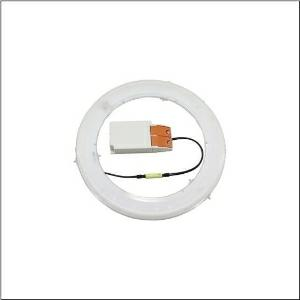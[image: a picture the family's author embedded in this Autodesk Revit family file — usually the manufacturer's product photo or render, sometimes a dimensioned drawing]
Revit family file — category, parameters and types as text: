
# Revit family: lunis_r_58dc011d04300a
name_source: partatom
category: Lighting Fixtures
units: mm (PartAtom-declared; Revit-internal decimal feet)

## family parameters
Cut with Voids When Loaded = No
Host = Face
Light Source = No
Part Type = Normal
Room Calculation Point = No
Round Connector Dimension = Use Diameter
Shared = No

## types (1)
- Lunis R (1 x LED, 4400 lm, 25.3 W, 4000K)
    Apparent Load = 25 VA
    CIE Flux Codes = 61 91 99 100 100
    Color Rendering = 80
    Color Temperature = 4000K
    Default Elevation = 1800 mm
    Description = Lunis R, luminaire insert, rated luminous flux: 4.400lm, light colour: 840, control gear: DALI 2, mains connection: 220..240V, AC, 50/60Hz, rated input power: 25W, primary light control with lens, of plastic, primary optical cover: cover, of PMMA, light emission: direct distribution, protection rating (complete): IP20, certification: CE, packaging unit: 1 piece
    Height = 70 mm
    Lamp = 1 x LED
    Lamp Light Flux = 4400 lm
    Lamp Power = 25.3 W
    Lamp count = 1
    Length = 398 mm
    Luminous efficacy = 174 lm/W
    Manufacturer = Siteco
    ModVariant = No
    Model = 58DC011D04300A
    Mounting Place = Ceiling
    Mounting Type = Surface mounted
    Number of Poles = 1
    OnlyDefault = Yes
    Power Factor = 1
    Product Name = Lunis R
    Product group = luminaire insert | ceiling mounted
    ProductGroupID = 300
    Protection Class = Protection class II
    Protection Degree = IP 20
    RLX_Detail_Level = 1
    RLX_Emergency_Light_Flux = 0 lm
    RLX_Emergency_Type = 0
    RLX_Emergency_Type_DB = No
    RlxData = <blob elided: 21653 chars, md5=f3f3906a>
    Socket = socket
    Standby Power = 0 W
    System Light Flux = 4400 lm
    System Power = 25 W
    Type Comments = Product without accessories
    Type Image = l_1372778.jpg
    URL = http://relux.com
    VarID = ---
    Voltage = 0 V
    Weight = 0.00 kg
    Width = 0 mm  [stored 0 ft]

note: [stored X ft] marks values corroborated as IEEE doubles in the binary element streams (Revit-internal decimal feet)

## geometry (parser evidence)
native form markers: Blend x4, Sweep x11
no freeform markers — native parametric forms only
